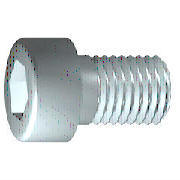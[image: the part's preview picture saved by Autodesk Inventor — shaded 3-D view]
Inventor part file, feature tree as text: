
AUTODESK INVENTOR PART (.ipt)
format: ipt  version: 2017 (Build 210142000, 142)  size: 184,832 bytes
history: native  units: mm (DEFAULTED — no unit token found)
features: sketch x2, extrude x1, plane x1, fillet x1
ambient origin geometry x7: Origin, YZ Plane, XY Plane, X Axis, Y Axis, Z Axis, Center Point
bodies: Solid1 (feature_tree), Body (feature_tree)
feature tree (5):
  extrude  "Slot"  Depth=4.0mm
  plane  "Work Plane1"
  fillet  "Fillet2"  Radius=4.0mm
  sketch  "Sketch1"  dims[d1=23.74117mm d2=0.429515mm d3=4.0mm]
  sketch  "Sketch2"  dims[d4=2.0mm d5=60.0deg d6=4.0mm d7=4.0mm d8=3.464102mm d9=7.0mm d10=90.0deg d11=10.0mm d12=0.0mm d13=23.74117mm d14=0.0mm d15=0.429415mm d16=0.429415mm d17=0.4mm d19=0.0mm d26=25.0mm d27=45.0deg d28=0.0mm d29=0.0mm d30=0.1mm]
